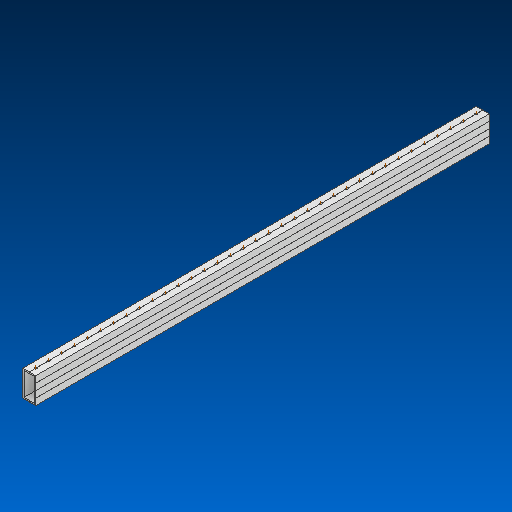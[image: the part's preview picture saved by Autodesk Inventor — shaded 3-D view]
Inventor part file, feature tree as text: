
AUTODESK INVENTOR PART (.ipt)
format: ipt  version: 2022.2 (Build 262287000, 287)  size: 536,576 bytes
history: native  units: in
note: dims shown in document units (in); Inventor stores cm internally (conversion verified against a paired STEP export)
features: other x36, extrude x1, pattern_linear x1, sketch x1
ambient origin geometry x8: Origin, YZ Plane, XZ Plane, XY Plane, X Axis, Y Axis, Z Axis, Center Point
bodies: Solid1 (feature_tree)
feature tree (39):
  extrude  "Extrusion1"  Depth=2.0in
  other  "Work Axis1"
  pattern_linear  "Rectangular Pattern1"  Spacing1=24.0in  [1 undecoded]
  sketch  "Sketch1"  dims[d0=1.0in d1=2.0in d2=24.0in d3=0.0in d4=13.7795in d6=1.0in]
  other  "Work Axis2"
  other  "Work Axis3"
  other  "Work Axis4"
  other  "Work Axis5"
  other  "Work Axis6"
  other  "Work Axis7"
  other  "Work Axis8"
  other  "Work Axis9"
  other  "Work Axis10"
  other  "Work Axis60"
  other  "Work Axis61"
  other  "Work Axis62"
  other  "Work Axis63"
  other  "Work Axis64"
  other  "Work Axis65"
  other  "Work Axis66"
  other  "Work Axis67"
  other  "Work Axis68"
  other  "Work Axis69"
  other  "Work Axis70"
  other  "Work Axis71"
  other  "Work Axis72"
  other  "Work Axis73"
  other  "Work Axis74"
  other  "Work Axis75"
  other  "Work Axis76"
  other  "Work Axis77"
  other  "Work Axis78"
  other  "Work Axis79"
  other  "Work Axis80"
  other  "Work Axis81"
  other  "Work Axis82"
  other  "Work Axis83"
  other  "Work Axis84"
  other  "Cut-Extrude2"
note: 1 required parameter value undecoded (feature->parameter linkage not recoverable at this tier; creation-order binding heuristic only, values carry confidence <= 0.55)
